# Revit family: DFM Doors - double leaf door OS without fire resistance
name_source: partatom
category: Doors
revit_build: Autodesk Revit 2017 (Build: 20190507_1515(x64)
units: mm (PartAtom-declared; Revit-internal decimal feet)

## family parameters
Always vertical = Yes
Cut with Voids When Loaded = No
Host = Wall
OmniClass Number = 23.30.10.00
OmniClass Title = Doors
Room Calculation Point = Yes
Shared = No

## types (1)
- 2500x2278.5 internal frame
    Additional hinge = No
    Clear opening height = 2500 mm  [stored 8.2021 ft]
    Clear opening height. Limiting dimensions = ok
    Clear opening width = 2278.5 mm  [stored 7.47539 ft]
    Clear opening width at opened active leaf = 1117.25 mm
    Clear opening width. Limiting dimensions = ok
    Corner frame = No
    Embracing frame = No
    Fire Rating = Without fire resistance
    Frame to frame width = 2331.5 mm  [stored 7.64928 ft]
    Function = Interior
    Height = 2572 mm  [stored 8.43832 ft]
    Height of the door leaf = 2520 mm  [stored 8.26772 ft]
    Internal frame = Yes
    Manufacturer = DFM Doors sp. z o. o.
    Material of astragal profie = DFM Doors - aluminium
    Material of cut-off for the ventilation grid KWZ = DFM Doors - cut-off for the ventilation grid 1
    Material of cut-off for the ventilation grid NV and ZET = DFM Doors - cut-off for the ventilation grid 2
    Material of door closer = DFM Doors - aluminium
    Material of door frame = DFM Doors - aluminium
    Material of door leaf = DFM Doors - zinc coated steel
    Material of drip cap = DFM Doors - zinc coated steel
    Material of glass = DFM Doors - glazing
    Material of glass framing = DFM Doors - zinc coated steel
    Material of hinges = DFM Doors - stainless steel
    Material of ironmongery = DFM Doors - aluminium
    Material of ventilation grid = DFM Doors - zinc coated steel
    Model = DFM OS 00 - 2
    Offset of the door leaf = 46 mm  [stored 0.150919 ft]
    Offset of the inter-leaf axis = 1237.75 mm  [stored 4.06086 ft]
    Offset of the passive active axis = 638.625 mm  [stored 2.09523 ft]
    Offset of the passive leaf axis = 638.625 mm  [stored 2.09523 ft]
    Rough Height = 2572 mm  [stored 8.43832 ft]
    Rough Width = 2475.5 mm
    Thickness = 65 mm  [stored 0.213255 ft]
    Type of frame = 2
    URL = https://www.dfm-europe.eu
    Wall Closure = By host
    Width = 2475.5 mm
    Width of active leaf = 1191.25 mm  [stored 3.9083 ft]
    Width of passive leaf = 1191.25 mm  [stored 3.9083 ft]

note: [stored X ft] marks values corroborated as IEEE doubles in the binary element streams (Revit-internal decimal feet)
